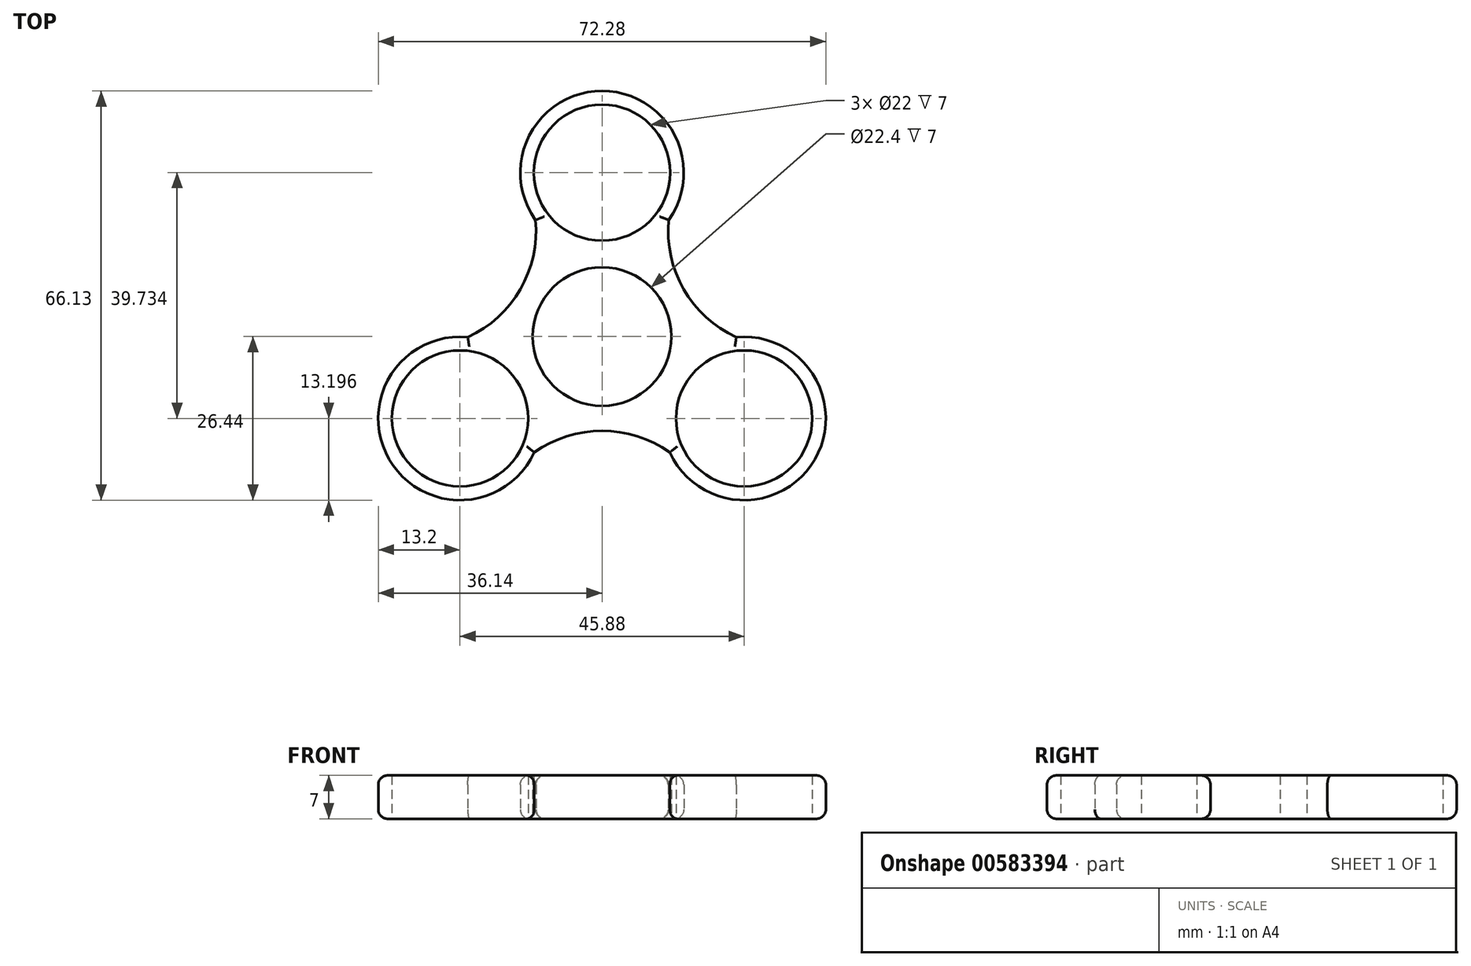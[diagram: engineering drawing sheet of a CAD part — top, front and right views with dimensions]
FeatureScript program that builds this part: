
annotation { "Feature Type Name" : "Feature", "Feature Type Description" : "" }
export const myFeature = defineFeature(function(context is Context, id is Id, definition is map)
    precondition{}
    {
        {
            var Q0;
            Q0=qCreatedBy(makeId("Top.planeOp"),FACE);
            var sketch = newSketch(context, id + "F0", { "sketchPlane" : qUnion([Q0])});
            skCircle(sketch, "E0", {"center": v(0, 0) * mm, "radius": 11.2 * mm});
            skCircle(sketch, "E1", {"center": v(0, 26.49) * mm, "radius": 11 * mm});
            skArc(sketch, "E2", {"start": v(10.75, 18.83) * mm, "mid": v(0, 39.69) * mm, "end": v(-10.75, 18.83) * mm});
            skCircle(sketch, "E3.1.0", {"center": v(-22.94, -13.24) * mm, "radius": 11 * mm});
            skArc(sketch, "E3.1.1", {"start": v(-21.69, -0.1) * mm, "mid": v(-34.37, -19.84) * mm, "end": v(-10.93, -18.73) * mm});
            skCircle(sketch, "E3.2.0", {"center": v(22.94, -13.24) * mm, "radius": 11 * mm});
            skArc(sketch, "E3.2.1", {"start": v(10.93, -18.73) * mm, "mid": v(34.37, -19.84) * mm, "end": v(21.69, -0.1) * mm});
            skArc(sketch, "E4", {"start": v(10.8, 19.24) * mm, "mid": v(13.1, 7.8) * mm, "end": v(21.69, -0.1) * mm});
            skArc(sketch, "E5.1.0", {"start": v(-22.06, -0.27) * mm, "mid": v(-13.3, 7.44) * mm, "end": v(-10.75, 18.83) * mm});
            skArc(sketch, "E5.2.0", {"start": v(11.26, -18.97) * mm, "mid": v(0.2, -15.24) * mm, "end": v(-10.93, -18.73) * mm});
            skSolve(sketch);
        }
        {
            var Q0;
            Q0 = qSketchRegion(id + "F0", true);
            extrude(context, id + "F1", {"entities" : qUnion([Q0]), "depth" : 7 * mm, "offsetDistance" : 25 * mm});
        }
        {
            var Q0;
            Q0=makeQuery(id+"F1.opExtrude","CAP_EDGE",EDGE,{"disambiguationData":[OSD([sQuery(id+"F0.wireOp",EDGE,"E5.2.0")])],"isStart":false});
            var Q1;
            Q1=makeQuery(id+"F1.opExtrude","CAP_EDGE",EDGE,{"disambiguationData":[OSD([sQuery(id+"F0.wireOp",EDGE,"E5.2.0")])],"isStart":true});
            fillet(context, id + "F2", {"entities" : qUnion([Q0, Q1]), "radius" : 1.5 * mm, "tangentPropagation" : true, "allowEdgeOverflow" : false});
        }
        {
            var Q0;
            Q0=makeQuery(id+"F1.opExtrude","CAP_EDGE",EDGE,{"disambiguationData":[OSD([sQuery(id+"F0.wireOp",EDGE,"E5.1.0")])],"isStart":false});
            var Q1;
            Q1=makeQuery(id+"F1.opExtrude","CAP_EDGE",EDGE,{"disambiguationData":[OSD([sQuery(id+"F0.wireOp",EDGE,"E5.1.0")])],"isStart":true});
            fillet(context, id + "F3", {"entities" : qUnion([Q0, Q1]), "radius" : 1.5 * mm, "tangentPropagation" : true, "allowEdgeOverflow" : false});
        }
        {
            var Q0;
            Q0=makeQuery(id+"F1.opExtrude","CAP_EDGE",EDGE,{"disambiguationData":[OSD([sQuery(id+"F0.wireOp",EDGE,"E4")])],"isStart":false});
            var Q1;
            Q1=makeQuery(id+"F1.opExtrude","CAP_EDGE",EDGE,{"disambiguationData":[OSD([sQuery(id+"F0.wireOp",EDGE,"E4")])],"isStart":true});
            fillet(context, id + "F4", {"entities" : qUnion([Q0, Q1]), "radius" : 1.5 * mm, "tangentPropagation" : true, "allowEdgeOverflow" : false});
        }
        {
            var Q0;
            Q0=makeQuery(id+"F1.opExtrude","CAP_EDGE",EDGE,{"disambiguationData":[OSD([sQuery(id+"F0.wireOp",EDGE,"E2")])],"isStart":false});
            var Q1;
            Q1=makeQuery(id+"F1.opExtrude","CAP_EDGE",EDGE,{"disambiguationData":[OSD([sQuery(id+"F0.wireOp",EDGE,"E3.1.1")])],"isStart":false});
            var Q2;
            {var subQ0=sQuery(id+"F0.wireOp",EDGE,"E5.1.0");Q2=makeQuery(id+"F3.opFillet","BLEND_EDGE",EDGE,{"blendedFrom":[makeQuery(id+"F1.opExtrude","CAP_EDGE",EDGE,{"disambiguationData":[OSD([subQ0])],"isStart":false}),makeQuery(id+"F1.opExtrude","CAP_FACE",FACE,{"disambiguationData":[OSD([sQuery(id+"F0.wireOp",EDGE,"E0"),sQuery(id+"F0.wireOp",EDGE,"E1"),sQuery(id+"F0.wireOp",EDGE,"E2"),sQuery(id+"F0.wireOp",EDGE,"E3.1.0"),sQuery(id+"F0.wireOp",EDGE,"E3.1.1"),sQuery(id+"F0.wireOp",EDGE,"E3.2.0"),sQuery(id+"F0.wireOp",EDGE,"E3.2.1"),sQuery(id+"F0.wireOp",EDGE,"E4"),subQ0,sQuery(id+"F0.wireOp",EDGE,"E5.2.0")])],"isStart":false})],"blendedInto":[makeQuery(id+"F1.opExtrude","CAP_FACE",FACE,{"disambiguationData":[OSD([sQuery(id+"F0.wireOp",EDGE,"E0"),sQuery(id+"F0.wireOp",EDGE,"E1"),sQuery(id+"F0.wireOp",EDGE,"E2"),sQuery(id+"F0.wireOp",EDGE,"E3.1.0"),sQuery(id+"F0.wireOp",EDGE,"E3.1.1"),sQuery(id+"F0.wireOp",EDGE,"E3.2.0"),sQuery(id+"F0.wireOp",EDGE,"E3.2.1"),sQuery(id+"F0.wireOp",EDGE,"E4"),subQ0,sQuery(id+"F0.wireOp",EDGE,"E5.2.0")])],"isStart":false})]});}
            var Q3;
            {var subQ0=sQuery(id+"F0.wireOp",EDGE,"E4");Q3=makeQuery(id+"F4.opFillet","BLEND_EDGE",EDGE,{"blendedFrom":[makeQuery(id+"F1.opExtrude","CAP_EDGE",EDGE,{"disambiguationData":[OSD([subQ0])],"isStart":false}),makeQuery(id+"F1.opExtrude","CAP_FACE",FACE,{"disambiguationData":[OSD([sQuery(id+"F0.wireOp",EDGE,"E0"),sQuery(id+"F0.wireOp",EDGE,"E1"),sQuery(id+"F0.wireOp",EDGE,"E2"),sQuery(id+"F0.wireOp",EDGE,"E3.1.0"),sQuery(id+"F0.wireOp",EDGE,"E3.1.1"),sQuery(id+"F0.wireOp",EDGE,"E3.2.0"),sQuery(id+"F0.wireOp",EDGE,"E3.2.1"),subQ0,sQuery(id+"F0.wireOp",EDGE,"E5.1.0"),sQuery(id+"F0.wireOp",EDGE,"E5.2.0")])],"isStart":false})],"blendedInto":[makeQuery(id+"F1.opExtrude","CAP_FACE",FACE,{"disambiguationData":[OSD([sQuery(id+"F0.wireOp",EDGE,"E0"),sQuery(id+"F0.wireOp",EDGE,"E1"),sQuery(id+"F0.wireOp",EDGE,"E2"),sQuery(id+"F0.wireOp",EDGE,"E3.1.0"),sQuery(id+"F0.wireOp",EDGE,"E3.1.1"),sQuery(id+"F0.wireOp",EDGE,"E3.2.0"),sQuery(id+"F0.wireOp",EDGE,"E3.2.1"),subQ0,sQuery(id+"F0.wireOp",EDGE,"E5.1.0"),sQuery(id+"F0.wireOp",EDGE,"E5.2.0")])],"isStart":false})]});}
            var Q4;
            Q4=makeQuery(id+"F1.opExtrude","CAP_EDGE",EDGE,{"disambiguationData":[OSD([sQuery(id+"F0.wireOp",EDGE,"E3.2.1")])],"isStart":false});
            var Q5;
            {var subQ0=sQuery(id+"F0.wireOp",EDGE,"E5.2.0");Q5=makeQuery(id+"F2.opFillet","BLEND_EDGE",EDGE,{"blendedFrom":[makeQuery(id+"F1.opExtrude","CAP_EDGE",EDGE,{"disambiguationData":[OSD([subQ0])],"isStart":false}),makeQuery(id+"F1.opExtrude","CAP_FACE",FACE,{"disambiguationData":[OSD([sQuery(id+"F0.wireOp",EDGE,"E0"),sQuery(id+"F0.wireOp",EDGE,"E1"),sQuery(id+"F0.wireOp",EDGE,"E2"),sQuery(id+"F0.wireOp",EDGE,"E3.1.0"),sQuery(id+"F0.wireOp",EDGE,"E3.1.1"),sQuery(id+"F0.wireOp",EDGE,"E3.2.0"),sQuery(id+"F0.wireOp",EDGE,"E3.2.1"),sQuery(id+"F0.wireOp",EDGE,"E4"),sQuery(id+"F0.wireOp",EDGE,"E5.1.0"),subQ0])],"isStart":false})],"blendedInto":[makeQuery(id+"F1.opExtrude","CAP_FACE",FACE,{"disambiguationData":[OSD([sQuery(id+"F0.wireOp",EDGE,"E0"),sQuery(id+"F0.wireOp",EDGE,"E1"),sQuery(id+"F0.wireOp",EDGE,"E2"),sQuery(id+"F0.wireOp",EDGE,"E3.1.0"),sQuery(id+"F0.wireOp",EDGE,"E3.1.1"),sQuery(id+"F0.wireOp",EDGE,"E3.2.0"),sQuery(id+"F0.wireOp",EDGE,"E3.2.1"),sQuery(id+"F0.wireOp",EDGE,"E4"),sQuery(id+"F0.wireOp",EDGE,"E5.1.0"),subQ0])],"isStart":false})]});}
            var Q6;
            {var subQ0=sQuery(id+"F0.wireOp",EDGE,"E5.2.0");Q6=makeQuery(id+"F2.opFillet","BLEND_EDGE",EDGE,{"blendedFrom":[makeQuery(id+"F1.opExtrude","CAP_EDGE",EDGE,{"disambiguationData":[OSD([subQ0])],"isStart":true}),makeQuery(id+"F1.opExtrude","SWEPT_FACE",FACE,{"disambiguationData":[OSD([subQ0])]})],"blendedInto":[makeQuery(id+"F1.opExtrude","SWEPT_FACE",FACE,{"disambiguationData":[OSD([subQ0])]})]});}
            fillet(context, id + "F5", {"entities" : qUnion([Q0, Q1, Q2, Q3, Q4, Q5, Q6]), "radius" : 1.5 * mm, "tangentPropagation" : true, "allowEdgeOverflow" : false});
        }
        {
            var Q0;
            Q0=makeQuery(id+"F1.opExtrude","CAP_EDGE",EDGE,{"disambiguationData":[OSD([sQuery(id+"F0.wireOp",EDGE,"E3.1.1")])],"isStart":true});
            var Q1;
            {var subQ0=sQuery(id+"F0.wireOp",EDGE,"E5.2.0");Q1=makeQuery(id+"F2.opFillet","BLEND_EDGE",EDGE,{"blendedFrom":[makeQuery(id+"F1.opExtrude","CAP_EDGE",EDGE,{"disambiguationData":[OSD([subQ0])],"isStart":true}),makeQuery(id+"F1.opExtrude","CAP_FACE",FACE,{"disambiguationData":[OSD([sQuery(id+"F0.wireOp",EDGE,"E0"),sQuery(id+"F0.wireOp",EDGE,"E1"),sQuery(id+"F0.wireOp",EDGE,"E2"),sQuery(id+"F0.wireOp",EDGE,"E3.1.0"),sQuery(id+"F0.wireOp",EDGE,"E3.1.1"),sQuery(id+"F0.wireOp",EDGE,"E3.2.0"),sQuery(id+"F0.wireOp",EDGE,"E3.2.1"),sQuery(id+"F0.wireOp",EDGE,"E4"),sQuery(id+"F0.wireOp",EDGE,"E5.1.0"),subQ0])],"isStart":true})],"blendedInto":[makeQuery(id+"F1.opExtrude","CAP_FACE",FACE,{"disambiguationData":[OSD([sQuery(id+"F0.wireOp",EDGE,"E0"),sQuery(id+"F0.wireOp",EDGE,"E1"),sQuery(id+"F0.wireOp",EDGE,"E2"),sQuery(id+"F0.wireOp",EDGE,"E3.1.0"),sQuery(id+"F0.wireOp",EDGE,"E3.1.1"),sQuery(id+"F0.wireOp",EDGE,"E3.2.0"),sQuery(id+"F0.wireOp",EDGE,"E3.2.1"),sQuery(id+"F0.wireOp",EDGE,"E4"),sQuery(id+"F0.wireOp",EDGE,"E5.1.0"),subQ0])],"isStart":true})]});}
            var Q2;
            Q2=makeQuery(id+"F1.opExtrude","CAP_EDGE",EDGE,{"disambiguationData":[OSD([sQuery(id+"F0.wireOp",EDGE,"E3.2.1")])],"isStart":true});
            var Q3;
            {var subQ0=sQuery(id+"F0.wireOp",EDGE,"E4");Q3=makeQuery(id+"F4.opFillet","BLEND_EDGE",EDGE,{"blendedFrom":[makeQuery(id+"F1.opExtrude","CAP_EDGE",EDGE,{"disambiguationData":[OSD([subQ0])],"isStart":true}),makeQuery(id+"F1.opExtrude","CAP_FACE",FACE,{"disambiguationData":[OSD([sQuery(id+"F0.wireOp",EDGE,"E0"),sQuery(id+"F0.wireOp",EDGE,"E1"),sQuery(id+"F0.wireOp",EDGE,"E2"),sQuery(id+"F0.wireOp",EDGE,"E3.1.0"),sQuery(id+"F0.wireOp",EDGE,"E3.1.1"),sQuery(id+"F0.wireOp",EDGE,"E3.2.0"),sQuery(id+"F0.wireOp",EDGE,"E3.2.1"),subQ0,sQuery(id+"F0.wireOp",EDGE,"E5.1.0"),sQuery(id+"F0.wireOp",EDGE,"E5.2.0")])],"isStart":true})],"blendedInto":[makeQuery(id+"F1.opExtrude","CAP_FACE",FACE,{"disambiguationData":[OSD([sQuery(id+"F0.wireOp",EDGE,"E0"),sQuery(id+"F0.wireOp",EDGE,"E1"),sQuery(id+"F0.wireOp",EDGE,"E2"),sQuery(id+"F0.wireOp",EDGE,"E3.1.0"),sQuery(id+"F0.wireOp",EDGE,"E3.1.1"),sQuery(id+"F0.wireOp",EDGE,"E3.2.0"),sQuery(id+"F0.wireOp",EDGE,"E3.2.1"),subQ0,sQuery(id+"F0.wireOp",EDGE,"E5.1.0"),sQuery(id+"F0.wireOp",EDGE,"E5.2.0")])],"isStart":true})]});}
            var Q4;
            Q4=makeQuery(id+"F1.opExtrude","CAP_EDGE",EDGE,{"disambiguationData":[OSD([sQuery(id+"F0.wireOp",EDGE,"E2")])],"isStart":true});
            var Q5;
            {var subQ0=sQuery(id+"F0.wireOp",EDGE,"E5.1.0");Q5=makeQuery(id+"F3.opFillet","BLEND_EDGE",EDGE,{"blendedFrom":[makeQuery(id+"F1.opExtrude","CAP_EDGE",EDGE,{"disambiguationData":[OSD([subQ0])],"isStart":true}),makeQuery(id+"F1.opExtrude","CAP_FACE",FACE,{"disambiguationData":[OSD([sQuery(id+"F0.wireOp",EDGE,"E0"),sQuery(id+"F0.wireOp",EDGE,"E1"),sQuery(id+"F0.wireOp",EDGE,"E2"),sQuery(id+"F0.wireOp",EDGE,"E3.1.0"),sQuery(id+"F0.wireOp",EDGE,"E3.1.1"),sQuery(id+"F0.wireOp",EDGE,"E3.2.0"),sQuery(id+"F0.wireOp",EDGE,"E3.2.1"),sQuery(id+"F0.wireOp",EDGE,"E4"),subQ0,sQuery(id+"F0.wireOp",EDGE,"E5.2.0")])],"isStart":true})],"blendedInto":[makeQuery(id+"F1.opExtrude","CAP_FACE",FACE,{"disambiguationData":[OSD([sQuery(id+"F0.wireOp",EDGE,"E0"),sQuery(id+"F0.wireOp",EDGE,"E1"),sQuery(id+"F0.wireOp",EDGE,"E2"),sQuery(id+"F0.wireOp",EDGE,"E3.1.0"),sQuery(id+"F0.wireOp",EDGE,"E3.1.1"),sQuery(id+"F0.wireOp",EDGE,"E3.2.0"),sQuery(id+"F0.wireOp",EDGE,"E3.2.1"),sQuery(id+"F0.wireOp",EDGE,"E4"),subQ0,sQuery(id+"F0.wireOp",EDGE,"E5.2.0")])],"isStart":true})]});}
            fillet(context, id + "F6", {"entities" : qUnion([Q0, Q1, Q2, Q3, Q4, Q5]), "radius" : 1.5 * mm, "tangentPropagation" : true, "allowEdgeOverflow" : false});
        }
    });
